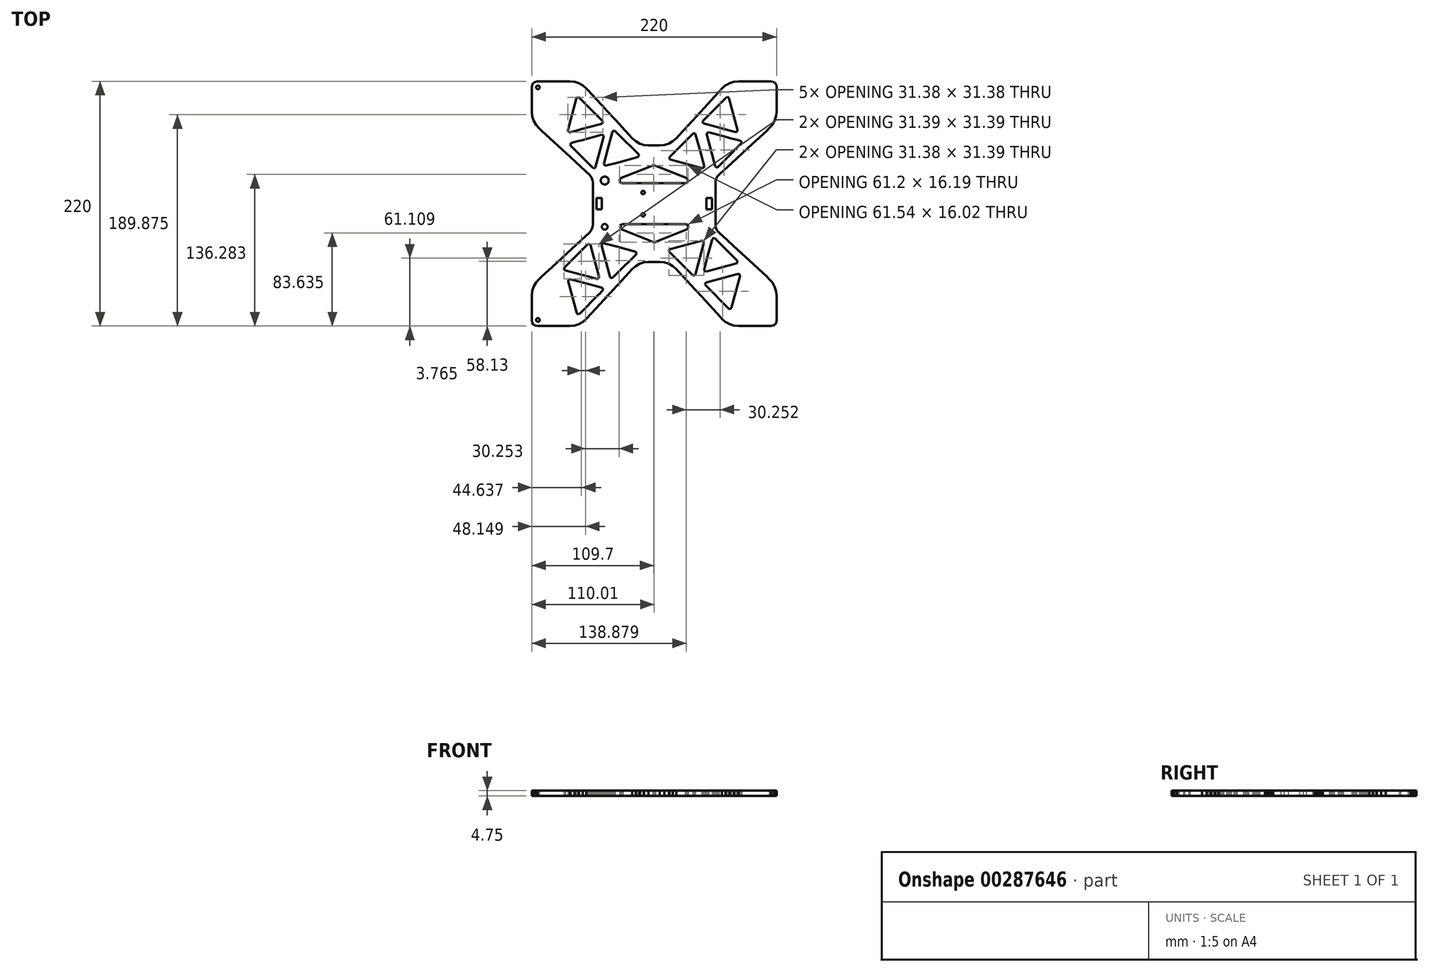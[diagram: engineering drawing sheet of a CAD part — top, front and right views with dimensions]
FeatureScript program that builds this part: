
annotation { "Feature Type Name" : "Feature", "Feature Type Description" : "" }
export const myFeature = defineFeature(function(context is Context, id is Id, definition is map)
    precondition{}
    {
        {
            var Q0;
            Q0=qCreatedBy(makeId("Top.planeOp"),FACE);
            var sketch = newSketch(context, id + "F0", { "sketchPlane" : qUnion([Q0])});
            skLineSegment(sketch, "E0", {"start": v(110, -105) * mm, "end": v(109.97, -105.11) * mm});
            skLineSegment(sketch, "E1", {"start": v(109.97, -105.11) * mm, "end": v(109.33, -107.5) * mm});
            skLineSegment(sketch, "E2", {"start": v(109.33, -107.5) * mm, "end": v(107.5, -109.33) * mm});
            skLineSegment(sketch, "E3", {"start": v(107.5, -109.33) * mm, "end": v(105.11, -109.97) * mm});
            skLineSegment(sketch, "E4", {"start": v(105.11, -109.97) * mm, "end": v(105, -110) * mm});
            skLineSegment(sketch, "E5", {"start": v(105, -110) * mm, "end": v(75.71, -110) * mm});
            skLineSegment(sketch, "E6", {"start": v(75.71, -110) * mm, "end": v(71.6, -109.58) * mm});
            skLineSegment(sketch, "E7", {"start": v(71.6, -109.58) * mm, "end": v(67.68, -108.32) * mm});
            skLineSegment(sketch, "E8", {"start": v(67.68, -108.32) * mm, "end": v(65.54, -107.1) * mm});
            skLineSegment(sketch, "E9", {"start": v(65.54, -107.1) * mm, "end": v(64.1, -106.29) * mm});
            skLineSegment(sketch, "E10", {"start": v(64.1, -106.29) * mm, "end": v(61, -103.56) * mm});
            skLineSegment(sketch, "E11", {"start": v(61, -103.56) * mm, "end": v(60.02, -102.49) * mm});
            skLineSegment(sketch, "E12", {"start": v(60.02, -102.49) * mm, "end": v(59.43, -101.85) * mm});
            skLineSegment(sketch, "E13", {"start": v(59.43, -101.85) * mm, "end": v(42.66, -83.66) * mm});
            skLineSegment(sketch, "E14", {"start": v(42.66, -83.66) * mm, "end": v(37.1, -77.62) * mm});
            skLineSegment(sketch, "E15", {"start": v(37.1, -77.62) * mm, "end": v(25.96, -65.54) * mm});
            skLineSegment(sketch, "E16", {"start": v(25.96, -65.54) * mm, "end": v(20.43, -59.54) * mm});
            skLineSegment(sketch, "E17", {"start": v(20.43, -59.54) * mm, "end": v(19.77, -58.82) * mm});
            skLineSegment(sketch, "E18", {"start": v(19.77, -58.82) * mm, "end": v(16.67, -56.1) * mm});
            skLineSegment(sketch, "E19", {"start": v(16.67, -56.1) * mm, "end": v(13.09, -54.06) * mm});
            skLineSegment(sketch, "E20", {"start": v(13.09, -54.06) * mm, "end": v(9.16, -52.8) * mm});
            skLineSegment(sketch, "E21", {"start": v(9.16, -52.8) * mm, "end": v(5.06, -52.37) * mm});
            skLineSegment(sketch, "E22", {"start": v(5.06, -52.37) * mm, "end": v(-5.06, -52.37) * mm});
            skLineSegment(sketch, "E23", {"start": v(-5.06, -52.37) * mm, "end": v(-9.16, -52.8) * mm});
            skLineSegment(sketch, "E24", {"start": v(-9.16, -52.8) * mm, "end": v(-13.1, -54.06) * mm});
            skLineSegment(sketch, "E25", {"start": v(-13.1, -54.06) * mm, "end": v(-16.67, -56.1) * mm});
            skLineSegment(sketch, "E26", {"start": v(-16.67, -56.1) * mm, "end": v(-19.77, -58.82) * mm});
            skLineSegment(sketch, "E27", {"start": v(-19.77, -58.82) * mm, "end": v(-25.96, -65.54) * mm});
            skLineSegment(sketch, "E28", {"start": v(-25.96, -65.54) * mm, "end": v(-32.77, -72.92) * mm});
            skLineSegment(sketch, "E29", {"start": v(-32.77, -72.92) * mm, "end": v(-37.77, -78.35) * mm});
            skLineSegment(sketch, "E30", {"start": v(-37.77, -78.35) * mm, "end": v(-38.62, -79.27) * mm});
            skLineSegment(sketch, "E31", {"start": v(-38.62, -79.27) * mm, "end": v(-39.42, -80.14) * mm});
            skLineSegment(sketch, "E32", {"start": v(-39.42, -80.14) * mm, "end": v(-41.06, -81.92) * mm});
            skLineSegment(sketch, "E33", {"start": v(-41.06, -81.92) * mm, "end": v(-56.16, -98.3) * mm});
            skLineSegment(sketch, "E34", {"start": v(-56.16, -98.3) * mm, "end": v(-61, -103.56) * mm});
            skLineSegment(sketch, "E35", {"start": v(-61, -103.56) * mm, "end": v(-64.1, -106.29) * mm});
            skLineSegment(sketch, "E36", {"start": v(-64.1, -106.29) * mm, "end": v(-65.54, -107.1) * mm});
            skLineSegment(sketch, "E37", {"start": v(-65.54, -107.1) * mm, "end": v(-67.68, -108.32) * mm});
            skLineSegment(sketch, "E38", {"start": v(-67.68, -108.32) * mm, "end": v(-71.6, -109.58) * mm});
            skLineSegment(sketch, "E39", {"start": v(-71.6, -109.58) * mm, "end": v(-75.71, -110) * mm});
            skLineSegment(sketch, "E40", {"start": v(-75.71, -110) * mm, "end": v(-105, -110) * mm});
            skLineSegment(sketch, "E41", {"start": v(-105, -110) * mm, "end": v(-106.91, -109.62) * mm});
            skLineSegment(sketch, "E42", {"start": v(-106.91, -109.62) * mm, "end": v(-108.53, -108.54) * mm});
            skLineSegment(sketch, "E43", {"start": v(-108.53, -108.54) * mm, "end": v(-109.62, -106.92) * mm});
            skLineSegment(sketch, "E44", {"start": v(-109.62, -106.92) * mm, "end": v(-110, -105) * mm});
            skLineSegment(sketch, "E45", {"start": v(-110, -105) * mm, "end": v(-110, -82.51) * mm});
            skLineSegment(sketch, "E46", {"start": v(-110, -82.51) * mm, "end": v(-109.58, -78.41) * mm});
            skLineSegment(sketch, "E47", {"start": v(-109.58, -78.41) * mm, "end": v(-108.32, -74.48) * mm});
            skLineSegment(sketch, "E48", {"start": v(-108.32, -74.48) * mm, "end": v(-106.28, -70.9) * mm});
            skLineSegment(sketch, "E49", {"start": v(-106.28, -70.9) * mm, "end": v(-103.55, -67.8) * mm});
            skLineSegment(sketch, "E50", {"start": v(-103.55, -67.8) * mm, "end": v(-101.1, -65.54) * mm});
            skLineSegment(sketch, "E51", {"start": v(-101.1, -65.54) * mm, "end": v(-91.63, -56.8) * mm});
            skLineSegment(sketch, "E52", {"start": v(-91.63, -56.8) * mm, "end": v(-65.54, -32.76) * mm});
            skLineSegment(sketch, "E53", {"start": v(-65.54, -32.76) * mm, "end": v(-58.22, -26.01) * mm});
            skLineSegment(sketch, "E54", {"start": v(-58.22, -26.01) * mm, "end": v(-56.86, -24.47) * mm});
            skLineSegment(sketch, "E55", {"start": v(-56.86, -24.47) * mm, "end": v(-55.84, -22.68) * mm});
            skLineSegment(sketch, "E56", {"start": v(-55.84, -22.68) * mm, "end": v(-55.21, -20.71) * mm});
            skLineSegment(sketch, "E57", {"start": v(-55.21, -20.71) * mm, "end": v(-55, -18.66) * mm});
            skLineSegment(sketch, "E58", {"start": v(-55, -18.66) * mm, "end": v(-55, 18.67) * mm});
            skLineSegment(sketch, "E59", {"start": v(-55, 18.67) * mm, "end": v(-55.21, 20.72) * mm});
            skLineSegment(sketch, "E60", {"start": v(-55.21, 20.72) * mm, "end": v(-55.84, 22.68) * mm});
            skLineSegment(sketch, "E61", {"start": v(-55.84, 22.68) * mm, "end": v(-56.86, 24.47) * mm});
            skLineSegment(sketch, "E62", {"start": v(-56.86, 24.47) * mm, "end": v(-58.22, 26.02) * mm});
            skLineSegment(sketch, "E63", {"start": v(-58.22, 26.02) * mm, "end": v(-65.54, 32.76) * mm});
            skLineSegment(sketch, "E64", {"start": v(-65.54, 32.76) * mm, "end": v(-66.26, 33.43) * mm});
            skLineSegment(sketch, "E65", {"start": v(-66.26, 33.43) * mm, "end": v(-75.44, 41.9) * mm});
            skLineSegment(sketch, "E66", {"start": v(-75.44, 41.9) * mm, "end": v(-101.1, 65.54) * mm});
            skLineSegment(sketch, "E67", {"start": v(-101.1, 65.54) * mm, "end": v(-103.55, 67.8) * mm});
            skLineSegment(sketch, "E68", {"start": v(-103.55, 67.8) * mm, "end": v(-106.28, 70.9) * mm});
            skLineSegment(sketch, "E69", {"start": v(-106.28, 70.9) * mm, "end": v(-108.32, 74.48) * mm});
            skLineSegment(sketch, "E70", {"start": v(-108.32, 74.48) * mm, "end": v(-109.58, 78.41) * mm});
            skLineSegment(sketch, "E71", {"start": v(-109.58, 78.41) * mm, "end": v(-110, 82.51) * mm});
            skLineSegment(sketch, "E72", {"start": v(-110, 82.51) * mm, "end": v(-110, 105) * mm});
            skLineSegment(sketch, "E73", {"start": v(-110, 105) * mm, "end": v(-109.97, 105.12) * mm});
            skLineSegment(sketch, "E74", {"start": v(-109.97, 105.12) * mm, "end": v(-109.33, 107.5) * mm});
            skLineSegment(sketch, "E75", {"start": v(-109.33, 107.5) * mm, "end": v(-108.87, 107.96) * mm});
            skLineSegment(sketch, "E76", {"start": v(-108.87, 107.96) * mm, "end": v(-107.5, 109.33) * mm});
            skLineSegment(sketch, "E77", {"start": v(-107.5, 109.33) * mm, "end": v(-105.11, 109.97) * mm});
            skLineSegment(sketch, "E78", {"start": v(-105.11, 109.97) * mm, "end": v(-105, 110) * mm});
            skLineSegment(sketch, "E79", {"start": v(-105, 110) * mm, "end": v(-75.71, 110) * mm});
            skLineSegment(sketch, "E80", {"start": v(-75.71, 110) * mm, "end": v(-71.6, 109.58) * mm});
            skLineSegment(sketch, "E81", {"start": v(-71.6, 109.58) * mm, "end": v(-67.68, 108.32) * mm});
            skLineSegment(sketch, "E82", {"start": v(-67.68, 108.32) * mm, "end": v(-65.54, 107.1) * mm});
            skLineSegment(sketch, "E83", {"start": v(-65.54, 107.1) * mm, "end": v(-64.1, 106.29) * mm});
            skLineSegment(sketch, "E84", {"start": v(-64.1, 106.29) * mm, "end": v(-61, 103.56) * mm});
            skLineSegment(sketch, "E85", {"start": v(-61, 103.56) * mm, "end": v(-59.4, 101.81) * mm});
            skLineSegment(sketch, "E86", {"start": v(-59.4, 101.81) * mm, "end": v(-43.95, 85.06) * mm});
            skLineSegment(sketch, "E87", {"start": v(-43.95, 85.06) * mm, "end": v(-42.3, 83.27) * mm});
            skLineSegment(sketch, "E88", {"start": v(-42.3, 83.27) * mm, "end": v(-34.8, 75.14) * mm});
            skLineSegment(sketch, "E89", {"start": v(-34.8, 75.14) * mm, "end": v(-25.96, 65.54) * mm});
            skLineSegment(sketch, "E90", {"start": v(-25.96, 65.54) * mm, "end": v(-19.77, 58.82) * mm});
            skLineSegment(sketch, "E91", {"start": v(-19.77, 58.82) * mm, "end": v(-16.67, 56.1) * mm});
            skLineSegment(sketch, "E92", {"start": v(-16.67, 56.1) * mm, "end": v(-13.1, 54.06) * mm});
            skLineSegment(sketch, "E93", {"start": v(-13.1, 54.06) * mm, "end": v(-9.16, 52.8) * mm});
            skLineSegment(sketch, "E94", {"start": v(-9.16, 52.8) * mm, "end": v(-5.06, 52.38) * mm});
            skLineSegment(sketch, "E95", {"start": v(-5.06, 52.38) * mm, "end": v(5.06, 52.38) * mm});
            skLineSegment(sketch, "E96", {"start": v(5.06, 52.38) * mm, "end": v(9.16, 52.8) * mm});
            skLineSegment(sketch, "E97", {"start": v(9.16, 52.8) * mm, "end": v(13.09, 54.06) * mm});
            skLineSegment(sketch, "E98", {"start": v(13.09, 54.06) * mm, "end": v(16.67, 56.1) * mm});
            skLineSegment(sketch, "E99", {"start": v(16.67, 56.1) * mm, "end": v(19.77, 58.82) * mm});
            skLineSegment(sketch, "E100", {"start": v(19.77, 58.82) * mm, "end": v(25.96, 65.54) * mm});
            skLineSegment(sketch, "E101", {"start": v(25.96, 65.54) * mm, "end": v(34.46, 74.76) * mm});
            skLineSegment(sketch, "E102", {"start": v(34.46, 74.76) * mm, "end": v(45, 86.2) * mm});
            skLineSegment(sketch, "E103", {"start": v(45, 86.2) * mm, "end": v(61, 103.56) * mm});
            skLineSegment(sketch, "E104", {"start": v(61, 103.56) * mm, "end": v(64.1, 106.29) * mm});
            skLineSegment(sketch, "E105", {"start": v(64.1, 106.29) * mm, "end": v(65.54, 107.1) * mm});
            skLineSegment(sketch, "E106", {"start": v(65.54, 107.1) * mm, "end": v(67.68, 108.32) * mm});
            skLineSegment(sketch, "E107", {"start": v(67.68, 108.32) * mm, "end": v(71.6, 109.58) * mm});
            skLineSegment(sketch, "E108", {"start": v(71.6, 109.58) * mm, "end": v(75.71, 110) * mm});
            skLineSegment(sketch, "E109", {"start": v(75.71, 110) * mm, "end": v(105, 110) * mm});
            skLineSegment(sketch, "E110", {"start": v(105, 110) * mm, "end": v(106.91, 109.62) * mm});
            skLineSegment(sketch, "E111", {"start": v(106.91, 109.62) * mm, "end": v(107.98, 108.9) * mm});
            skLineSegment(sketch, "E112", {"start": v(107.98, 108.9) * mm, "end": v(108.53, 108.54) * mm});
            skLineSegment(sketch, "E113", {"start": v(108.53, 108.54) * mm, "end": v(109.62, 106.92) * mm});
            skLineSegment(sketch, "E114", {"start": v(109.62, 106.92) * mm, "end": v(109.98, 105.13) * mm});
            skLineSegment(sketch, "E115", {"start": v(109.98, 105.13) * mm, "end": v(110, 105) * mm});
            skLineSegment(sketch, "E116", {"start": v(110, 105) * mm, "end": v(110, 82.51) * mm});
            skLineSegment(sketch, "E117", {"start": v(110, 82.51) * mm, "end": v(109.58, 78.41) * mm});
            skLineSegment(sketch, "E118", {"start": v(109.58, 78.41) * mm, "end": v(108.32, 74.48) * mm});
            skLineSegment(sketch, "E119", {"start": v(108.32, 74.48) * mm, "end": v(106.28, 70.9) * mm});
            skLineSegment(sketch, "E120", {"start": v(106.28, 70.9) * mm, "end": v(103.56, 67.8) * mm});
            skLineSegment(sketch, "E121", {"start": v(103.56, 67.8) * mm, "end": v(101.1, 65.54) * mm});
            skLineSegment(sketch, "E122", {"start": v(101.1, 65.54) * mm, "end": v(88.12, 53.58) * mm});
            skLineSegment(sketch, "E123", {"start": v(88.12, 53.58) * mm, "end": v(65.54, 32.76) * mm});
            skLineSegment(sketch, "E124", {"start": v(65.54, 32.76) * mm, "end": v(63.4, 30.8) * mm});
            skLineSegment(sketch, "E125", {"start": v(63.4, 30.8) * mm, "end": v(58.22, 26.02) * mm});
            skLineSegment(sketch, "E126", {"start": v(58.22, 26.02) * mm, "end": v(56.86, 24.47) * mm});
            skLineSegment(sketch, "E127", {"start": v(56.86, 24.47) * mm, "end": v(55.84, 22.68) * mm});
            skLineSegment(sketch, "E128", {"start": v(55.84, 22.68) * mm, "end": v(55.21, 20.72) * mm});
            skLineSegment(sketch, "E129", {"start": v(55.21, 20.72) * mm, "end": v(55, 18.67) * mm});
            skLineSegment(sketch, "E130", {"start": v(55, 18.67) * mm, "end": v(55, -18.66) * mm});
            skLineSegment(sketch, "E131", {"start": v(55, -18.66) * mm, "end": v(55.21, -20.71) * mm});
            skLineSegment(sketch, "E132", {"start": v(55.21, -20.71) * mm, "end": v(55.84, -22.68) * mm});
            skLineSegment(sketch, "E133", {"start": v(55.84, -22.68) * mm, "end": v(56.86, -24.47) * mm});
            skLineSegment(sketch, "E134", {"start": v(56.86, -24.47) * mm, "end": v(58.22, -26.01) * mm});
            skLineSegment(sketch, "E135", {"start": v(58.22, -26.01) * mm, "end": v(65.54, -32.76) * mm});
            skLineSegment(sketch, "E136", {"start": v(65.54, -32.76) * mm, "end": v(66.29, -33.45) * mm});
            skLineSegment(sketch, "E137", {"start": v(66.29, -33.45) * mm, "end": v(75, -41.48) * mm});
            skLineSegment(sketch, "E138", {"start": v(75, -41.48) * mm, "end": v(81.72, -47.68) * mm});
            skLineSegment(sketch, "E139", {"start": v(81.72, -47.68) * mm, "end": v(101.1, -65.54) * mm});
            skLineSegment(sketch, "E140", {"start": v(101.1, -65.54) * mm, "end": v(103.56, -67.8) * mm});
            skLineSegment(sketch, "E141", {"start": v(103.56, -67.8) * mm, "end": v(106.28, -70.9) * mm});
            skLineSegment(sketch, "E142", {"start": v(106.28, -70.9) * mm, "end": v(108.32, -74.48) * mm});
            skLineSegment(sketch, "E143", {"start": v(108.32, -74.48) * mm, "end": v(109.58, -78.41) * mm});
            skLineSegment(sketch, "E144", {"start": v(109.58, -78.41) * mm, "end": v(110, -82.51) * mm});
            skLineSegment(sketch, "E145", {"start": v(110, -82.51) * mm, "end": v(110, -105) * mm});
            skLineSegment(sketch, "E146", {"start": v(-43.2, 34.18) * mm, "end": v(-32.77, 36.98) * mm});
            skLineSegment(sketch, "E147", {"start": v(-32.77, 36.98) * mm, "end": v(-14.76, 41.8) * mm});
            skLineSegment(sketch, "E148", {"start": v(-14.76, 41.8) * mm, "end": v(-13.92, 42.4) * mm});
            skLineSegment(sketch, "E149", {"start": v(-13.92, 42.4) * mm, "end": v(-13.66, 43.38) * mm});
            skLineSegment(sketch, "E150", {"start": v(-13.66, 43.38) * mm, "end": v(-14.1, 44.31) * mm});
            skLineSegment(sketch, "E151", {"start": v(-14.1, 44.31) * mm, "end": v(-32.77, 62.99) * mm});
            skLineSegment(sketch, "E152", {"start": v(-32.77, 62.99) * mm, "end": v(-34.9, 65.12) * mm});
            skLineSegment(sketch, "E153", {"start": v(-34.9, 65.12) * mm, "end": v(-34.91, 65.13) * mm});
            skLineSegment(sketch, "E154", {"start": v(-34.91, 65.13) * mm, "end": v(-35.78, 65.54) * mm});
            skLineSegment(sketch, "E155", {"start": v(-35.78, 65.54) * mm, "end": v(-35.84, 65.57) * mm});
            skLineSegment(sketch, "E156", {"start": v(-35.84, 65.57) * mm, "end": v(-35.95, 65.54) * mm});
            skLineSegment(sketch, "E157", {"start": v(-35.95, 65.54) * mm, "end": v(-36.83, 65.3) * mm});
            skLineSegment(sketch, "E158", {"start": v(-36.83, 65.3) * mm, "end": v(-37.42, 64.46) * mm});
            skLineSegment(sketch, "E159", {"start": v(-37.42, 64.46) * mm, "end": v(-37.43, 64.44) * mm});
            skLineSegment(sketch, "E160", {"start": v(-37.43, 64.44) * mm, "end": v(-41.52, 49.15) * mm});
            skLineSegment(sketch, "E161", {"start": v(-41.52, 49.15) * mm, "end": v(-45.04, 36.02) * mm});
            skLineSegment(sketch, "E162", {"start": v(-45.04, 36.02) * mm, "end": v(-44.95, 35) * mm});
            skLineSegment(sketch, "E163", {"start": v(-44.95, 35) * mm, "end": v(-44.23, 34.27) * mm});
            skLineSegment(sketch, "E164", {"start": v(-44.23, 34.27) * mm, "end": v(-43.2, 34.18) * mm});
            skLineSegment(sketch, "E165", {"start": v(-58.87, -36.18) * mm, "end": v(-59.8, -36.61) * mm});
            skLineSegment(sketch, "E166", {"start": v(-59.8, -36.61) * mm, "end": v(-65.54, -42.35) * mm});
            skLineSegment(sketch, "E167", {"start": v(-65.54, -42.35) * mm, "end": v(-80.62, -57.43) * mm});
            skLineSegment(sketch, "E168", {"start": v(-80.62, -57.43) * mm, "end": v(-81.06, -58.36) * mm});
            skLineSegment(sketch, "E169", {"start": v(-81.06, -58.36) * mm, "end": v(-80.79, -59.35) * mm});
            skLineSegment(sketch, "E170", {"start": v(-80.79, -59.35) * mm, "end": v(-79.95, -59.94) * mm});
            skLineSegment(sketch, "E171", {"start": v(-79.95, -59.94) * mm, "end": v(-65.54, -63.8) * mm});
            skLineSegment(sketch, "E172", {"start": v(-65.54, -63.8) * mm, "end": v(-59.07, -65.54) * mm});
            skLineSegment(sketch, "E173", {"start": v(-59.07, -65.54) * mm, "end": v(-51.5, -67.56) * mm});
            skLineSegment(sketch, "E174", {"start": v(-51.5, -67.56) * mm, "end": v(-50.49, -67.47) * mm});
            skLineSegment(sketch, "E175", {"start": v(-50.49, -67.47) * mm, "end": v(-49.76, -66.75) * mm});
            skLineSegment(sketch, "E176", {"start": v(-49.76, -66.75) * mm, "end": v(-49.67, -65.73) * mm});
            skLineSegment(sketch, "E177", {"start": v(-49.67, -65.73) * mm, "end": v(-49.72, -65.54) * mm});
            skLineSegment(sketch, "E178", {"start": v(-49.72, -65.54) * mm, "end": v(-49.74, -65.46) * mm});
            skLineSegment(sketch, "E179", {"start": v(-49.74, -65.46) * mm, "end": v(-55.38, -44.43) * mm});
            skLineSegment(sketch, "E180", {"start": v(-55.38, -44.43) * mm, "end": v(-57.3, -37.28) * mm});
            skLineSegment(sketch, "E181", {"start": v(-57.3, -37.28) * mm, "end": v(-57.81, -36.53) * mm});
            skLineSegment(sketch, "E182", {"start": v(-57.81, -36.53) * mm, "end": v(-57.88, -36.44) * mm});
            skLineSegment(sketch, "E183", {"start": v(-57.88, -36.44) * mm, "end": v(-58.87, -36.18) * mm});
            skLineSegment(sketch, "E184", {"start": v(65.54, 66.43) * mm, "end": v(68.87, 65.54) * mm});
            skLineSegment(sketch, "E185", {"start": v(68.87, 65.54) * mm, "end": v(72.99, 64.43) * mm});
            skLineSegment(sketch, "E186", {"start": v(72.99, 64.43) * mm, "end": v(74, 64.52) * mm});
            skLineSegment(sketch, "E187", {"start": v(74, 64.52) * mm, "end": v(74.73, 65.25) * mm});
            skLineSegment(sketch, "E188", {"start": v(74.73, 65.25) * mm, "end": v(74.76, 65.54) * mm});
            skLineSegment(sketch, "E189", {"start": v(74.76, 65.54) * mm, "end": v(74.82, 66.27) * mm});
            skLineSegment(sketch, "E190", {"start": v(74.82, 66.27) * mm, "end": v(67.2, 94.71) * mm});
            skLineSegment(sketch, "E191", {"start": v(67.2, 94.71) * mm, "end": v(66.62, 95.55) * mm});
            skLineSegment(sketch, "E192", {"start": v(66.62, 95.55) * mm, "end": v(65.62, 95.82) * mm});
            skLineSegment(sketch, "E193", {"start": v(65.62, 95.82) * mm, "end": v(65.54, 95.78) * mm});
            skLineSegment(sketch, "E194", {"start": v(65.54, 95.78) * mm, "end": v(64.7, 95.39) * mm});
            skLineSegment(sketch, "E195", {"start": v(64.7, 95.39) * mm, "end": v(43.87, 74.57) * mm});
            skLineSegment(sketch, "E196", {"start": v(43.87, 74.57) * mm, "end": v(43.44, 73.64) * mm});
            skLineSegment(sketch, "E197", {"start": v(43.44, 73.64) * mm, "end": v(43.7, 72.65) * mm});
            skLineSegment(sketch, "E198", {"start": v(43.7, 72.65) * mm, "end": v(44.55, 72.06) * mm});
            skLineSegment(sketch, "E199", {"start": v(44.55, 72.06) * mm, "end": v(65.54, 66.43) * mm});
            skLineSegment(sketch, "E200", {"start": v(-17.01, -43.07) * mm, "end": v(-32.77, -38.85) * mm});
            skLineSegment(sketch, "E201", {"start": v(-32.77, -38.85) * mm, "end": v(-45.45, -35.45) * mm});
            skLineSegment(sketch, "E202", {"start": v(-45.45, -35.45) * mm, "end": v(-46.48, -35.54) * mm});
            skLineSegment(sketch, "E203", {"start": v(-46.48, -35.54) * mm, "end": v(-47.2, -36.26) * mm});
            skLineSegment(sketch, "E204", {"start": v(-47.2, -36.26) * mm, "end": v(-47.3, -37.28) * mm});
            skLineSegment(sketch, "E205", {"start": v(-47.3, -37.28) * mm, "end": v(-39.72, -65.54) * mm});
            skLineSegment(sketch, "E206", {"start": v(-39.72, -65.54) * mm, "end": v(-39.67, -65.73) * mm});
            skLineSegment(sketch, "E207", {"start": v(-39.67, -65.73) * mm, "end": v(-39.08, -66.57) * mm});
            skLineSegment(sketch, "E208", {"start": v(-39.08, -66.57) * mm, "end": v(-38.1, -66.83) * mm});
            skLineSegment(sketch, "E209", {"start": v(-38.1, -66.83) * mm, "end": v(-37.16, -66.4) * mm});
            skLineSegment(sketch, "E210", {"start": v(-37.16, -66.4) * mm, "end": v(-36.3, -65.54) * mm});
            skLineSegment(sketch, "E211", {"start": v(-36.3, -65.54) * mm, "end": v(-32.77, -62) * mm});
            skLineSegment(sketch, "E212", {"start": v(-32.77, -62) * mm, "end": v(-16.34, -45.58) * mm});
            skLineSegment(sketch, "E213", {"start": v(-16.34, -45.58) * mm, "end": v(-15.9, -44.65) * mm});
            skLineSegment(sketch, "E214", {"start": v(-15.9, -44.65) * mm, "end": v(-16.17, -43.65) * mm});
            skLineSegment(sketch, "E215", {"start": v(-16.17, -43.65) * mm, "end": v(-17.01, -43.07) * mm});
            skLineSegment(sketch, "E216", {"start": v(78.32, 55.84) * mm, "end": v(77.48, 56.43) * mm});
            skLineSegment(sketch, "E217", {"start": v(77.48, 56.43) * mm, "end": v(74.05, 57.35) * mm});
            skLineSegment(sketch, "E218", {"start": v(74.05, 57.35) * mm, "end": v(68.35, 58.88) * mm});
            skLineSegment(sketch, "E219", {"start": v(68.35, 58.88) * mm, "end": v(65.54, 59.63) * mm});
            skLineSegment(sketch, "E220", {"start": v(65.54, 59.63) * mm, "end": v(49.04, 64.05) * mm});
            skLineSegment(sketch, "E221", {"start": v(49.04, 64.05) * mm, "end": v(48.02, 63.96) * mm});
            skLineSegment(sketch, "E222", {"start": v(48.02, 63.96) * mm, "end": v(47.3, 63.24) * mm});
            skLineSegment(sketch, "E223", {"start": v(47.3, 63.24) * mm, "end": v(47.2, 62.21) * mm});
            skLineSegment(sketch, "E224", {"start": v(47.2, 62.21) * mm, "end": v(50.7, 49.15) * mm});
            skLineSegment(sketch, "E225", {"start": v(50.7, 49.15) * mm, "end": v(54.82, 33.77) * mm});
            skLineSegment(sketch, "E226", {"start": v(54.82, 33.77) * mm, "end": v(55.41, 32.93) * mm});
            skLineSegment(sketch, "E227", {"start": v(55.41, 32.93) * mm, "end": v(56.02, 32.77) * mm});
            skLineSegment(sketch, "E228", {"start": v(56.02, 32.77) * mm, "end": v(56.4, 32.66) * mm});
            skLineSegment(sketch, "E229", {"start": v(56.4, 32.66) * mm, "end": v(56.62, 32.77) * mm});
            skLineSegment(sketch, "E230", {"start": v(56.62, 32.77) * mm, "end": v(57.33, 33.1) * mm});
            skLineSegment(sketch, "E231", {"start": v(57.33, 33.1) * mm, "end": v(65.54, 41.3) * mm});
            skLineSegment(sketch, "E232", {"start": v(65.54, 41.3) * mm, "end": v(78.16, 53.92) * mm});
            skLineSegment(sketch, "E233", {"start": v(78.16, 53.92) * mm, "end": v(78.59, 54.85) * mm});
            skLineSegment(sketch, "E234", {"start": v(78.59, 54.85) * mm, "end": v(78.32, 55.84) * mm});
            skLineSegment(sketch, "E235", {"start": v(-53.26, 32.1) * mm, "end": v(-52.79, 32.77) * mm});
            skLineSegment(sketch, "E236", {"start": v(-52.79, 32.77) * mm, "end": v(-52.67, 32.94) * mm});
            skLineSegment(sketch, "E237", {"start": v(-52.67, 32.94) * mm, "end": v(-48.33, 49.15) * mm});
            skLineSegment(sketch, "E238", {"start": v(-48.33, 49.15) * mm, "end": v(-45.43, 59.97) * mm});
            skLineSegment(sketch, "E239", {"start": v(-45.43, 59.97) * mm, "end": v(-45.52, 60.99) * mm});
            skLineSegment(sketch, "E240", {"start": v(-45.52, 60.99) * mm, "end": v(-46.24, 61.71) * mm});
            skLineSegment(sketch, "E241", {"start": v(-46.24, 61.71) * mm, "end": v(-47.26, 61.8) * mm});
            skLineSegment(sketch, "E242", {"start": v(-47.26, 61.8) * mm, "end": v(-65.54, 56.9) * mm});
            skLineSegment(sketch, "E243", {"start": v(-65.54, 56.9) * mm, "end": v(-68.56, 56.1) * mm});
            skLineSegment(sketch, "E244", {"start": v(-68.56, 56.1) * mm, "end": v(-74.3, 54.56) * mm});
            skLineSegment(sketch, "E245", {"start": v(-74.3, 54.56) * mm, "end": v(-75.13, 53.97) * mm});
            skLineSegment(sketch, "E246", {"start": v(-75.13, 53.97) * mm, "end": v(-75.4, 52.98) * mm});
            skLineSegment(sketch, "E247", {"start": v(-75.4, 52.98) * mm, "end": v(-74.96, 52.05) * mm});
            skLineSegment(sketch, "E248", {"start": v(-74.96, 52.05) * mm, "end": v(-65.54, 42.63) * mm});
            skLineSegment(sketch, "E249", {"start": v(-65.54, 42.63) * mm, "end": v(-55.68, 32.77) * mm});
            skLineSegment(sketch, "E250", {"start": v(-55.68, 32.77) * mm, "end": v(-55.18, 32.27) * mm});
            skLineSegment(sketch, "E251", {"start": v(-55.18, 32.27) * mm, "end": v(-54.25, 31.83) * mm});
            skLineSegment(sketch, "E252", {"start": v(-54.25, 31.83) * mm, "end": v(-53.26, 32.1) * mm});
            skLineSegment(sketch, "E253", {"start": v(-75.7, 64.18) * mm, "end": v(-70.65, 65.54) * mm});
            skLineSegment(sketch, "E254", {"start": v(-70.65, 65.54) * mm, "end": v(-65.54, 66.9) * mm});
            skLineSegment(sketch, "E255", {"start": v(-65.54, 66.9) * mm, "end": v(-48.52, 71.47) * mm});
            skLineSegment(sketch, "E256", {"start": v(-48.52, 71.47) * mm, "end": v(-47.26, 71.8) * mm});
            skLineSegment(sketch, "E257", {"start": v(-47.26, 71.8) * mm, "end": v(-46.42, 72.4) * mm});
            skLineSegment(sketch, "E258", {"start": v(-46.42, 72.4) * mm, "end": v(-46.16, 73.38) * mm});
            skLineSegment(sketch, "E259", {"start": v(-46.16, 73.38) * mm, "end": v(-46.6, 74.31) * mm});
            skLineSegment(sketch, "E260", {"start": v(-46.6, 74.31) * mm, "end": v(-67.41, 95.13) * mm});
            skLineSegment(sketch, "E261", {"start": v(-67.41, 95.13) * mm, "end": v(-68.34, 95.57) * mm});
            skLineSegment(sketch, "E262", {"start": v(-68.34, 95.57) * mm, "end": v(-69.33, 95.3) * mm});
            skLineSegment(sketch, "E263", {"start": v(-69.33, 95.3) * mm, "end": v(-69.92, 94.46) * mm});
            skLineSegment(sketch, "E264", {"start": v(-69.92, 94.46) * mm, "end": v(-77.54, 66.02) * mm});
            skLineSegment(sketch, "E265", {"start": v(-77.54, 66.02) * mm, "end": v(-77.5, 65.54) * mm});
            skLineSegment(sketch, "E266", {"start": v(-77.5, 65.54) * mm, "end": v(-77.45, 65) * mm});
            skLineSegment(sketch, "E267", {"start": v(-77.45, 65) * mm, "end": v(-76.73, 64.27) * mm});
            skLineSegment(sketch, "E268", {"start": v(-76.73, 64.27) * mm, "end": v(-75.7, 64.18) * mm});
            skLineSegment(sketch, "E269", {"start": v(30.35, -22.02) * mm, "end": v(30.61, -20.32) * mm});
            skLineSegment(sketch, "E270", {"start": v(30.61, -20.32) * mm, "end": v(29.73, -18.85) * mm});
            skLineSegment(sketch, "E271", {"start": v(29.73, -18.85) * mm, "end": v(28.12, -18.27) * mm});
            skLineSegment(sketch, "E272", {"start": v(28.12, -18.27) * mm, "end": v(-28.1, -18.27) * mm});
            skLineSegment(sketch, "E273", {"start": v(-28.1, -18.27) * mm, "end": v(-29.72, -18.85) * mm});
            skLineSegment(sketch, "E274", {"start": v(-29.72, -18.85) * mm, "end": v(-30.6, -20.33) * mm});
            skLineSegment(sketch, "E275", {"start": v(-30.6, -20.33) * mm, "end": v(-30.33, -22.02) * mm});
            skLineSegment(sketch, "E276", {"start": v(-30.33, -22.02) * mm, "end": v(-29.04, -23.16) * mm});
            skLineSegment(sketch, "E277", {"start": v(-29.04, -23.16) * mm, "end": v(-5.1, -32.77) * mm});
            skLineSegment(sketch, "E278", {"start": v(-5.1, -32.77) * mm, "end": v(-3.98, -33.22) * mm});
            skLineSegment(sketch, "E279", {"start": v(-3.98, -33.22) * mm, "end": v(-0.88, -34.46) * mm});
            skLineSegment(sketch, "E280", {"start": v(-0.88, -34.46) * mm, "end": v(0, -34.46) * mm});
            skLineSegment(sketch, "E281", {"start": v(0, -34.46) * mm, "end": v(1.01, -34.46) * mm});
            skLineSegment(sketch, "E282", {"start": v(1.01, -34.46) * mm, "end": v(3.68, -33.39) * mm});
            skLineSegment(sketch, "E283", {"start": v(3.68, -33.39) * mm, "end": v(5.22, -32.77) * mm});
            skLineSegment(sketch, "E284", {"start": v(5.22, -32.77) * mm, "end": v(29.07, -23.16) * mm});
            skLineSegment(sketch, "E285", {"start": v(29.07, -23.16) * mm, "end": v(30.35, -22.02) * mm});
            skLineSegment(sketch, "E286", {"start": v(-52, 5) * mm, "end": v(-52, -5) * mm});
            skLineSegment(sketch, "E287", {"start": v(-52, -5) * mm, "end": v(-47, -5) * mm});
            skLineSegment(sketch, "E288", {"start": v(-47, -5) * mm, "end": v(-47, 5) * mm});
            skLineSegment(sketch, "E289", {"start": v(-47, 5) * mm, "end": v(-52, 5) * mm});
            skLineSegment(sketch, "E290", {"start": v(75.23, -63.2) * mm, "end": v(66.52, -65.54) * mm});
            skLineSegment(sketch, "E291", {"start": v(66.52, -65.54) * mm, "end": v(65.54, -65.8) * mm});
            skLineSegment(sketch, "E292", {"start": v(65.54, -65.8) * mm, "end": v(46.8, -70.82) * mm});
            skLineSegment(sketch, "E293", {"start": v(46.8, -70.82) * mm, "end": v(45.95, -71.4) * mm});
            skLineSegment(sketch, "E294", {"start": v(45.95, -71.4) * mm, "end": v(45.69, -72.4) * mm});
            skLineSegment(sketch, "E295", {"start": v(45.69, -72.4) * mm, "end": v(46.12, -73.33) * mm});
            skLineSegment(sketch, "E296", {"start": v(46.12, -73.33) * mm, "end": v(66.94, -94.15) * mm});
            skLineSegment(sketch, "E297", {"start": v(66.94, -94.15) * mm, "end": v(67.87, -94.58) * mm});
            skLineSegment(sketch, "E298", {"start": v(67.87, -94.58) * mm, "end": v(68.86, -94.32) * mm});
            skLineSegment(sketch, "E299", {"start": v(68.86, -94.32) * mm, "end": v(69.45, -93.48) * mm});
            skLineSegment(sketch, "E300", {"start": v(69.45, -93.48) * mm, "end": v(76.94, -65.54) * mm});
            skLineSegment(sketch, "E301", {"start": v(76.94, -65.54) * mm, "end": v(77.07, -65.04) * mm});
            skLineSegment(sketch, "E302", {"start": v(77.07, -65.04) * mm, "end": v(76.98, -64.01) * mm});
            skLineSegment(sketch, "E303", {"start": v(76.98, -64.01) * mm, "end": v(76.26, -63.29) * mm});
            skLineSegment(sketch, "E304", {"start": v(76.26, -63.29) * mm, "end": v(75.23, -63.2) * mm});
            skLineSegment(sketch, "E305", {"start": v(-46.17, -76.16) * mm, "end": v(-46.61, -75.85) * mm});
            skLineSegment(sketch, "E306", {"start": v(-46.61, -75.85) * mm, "end": v(-47.01, -75.57) * mm});
            skLineSegment(sketch, "E307", {"start": v(-47.01, -75.57) * mm, "end": v(-49.15, -75) * mm});
            skLineSegment(sketch, "E308", {"start": v(-49.15, -75) * mm, "end": v(-65.54, -70.6) * mm});
            skLineSegment(sketch, "E309", {"start": v(-65.54, -70.6) * mm, "end": v(-75.45, -67.95) * mm});
            skLineSegment(sketch, "E310", {"start": v(-75.45, -67.95) * mm, "end": v(-76.48, -68.04) * mm});
            skLineSegment(sketch, "E311", {"start": v(-76.48, -68.04) * mm, "end": v(-77.2, -68.76) * mm});
            skLineSegment(sketch, "E312", {"start": v(-77.2, -68.76) * mm, "end": v(-77.3, -69.79) * mm});
            skLineSegment(sketch, "E313", {"start": v(-77.3, -69.79) * mm, "end": v(-69.67, -98.23) * mm});
            skLineSegment(sketch, "E314", {"start": v(-69.67, -98.23) * mm, "end": v(-69.61, -98.3) * mm});
            skLineSegment(sketch, "E315", {"start": v(-69.61, -98.3) * mm, "end": v(-69.08, -99.07) * mm});
            skLineSegment(sketch, "E316", {"start": v(-69.08, -99.07) * mm, "end": v(-68.1, -99.33) * mm});
            skLineSegment(sketch, "E317", {"start": v(-68.1, -99.33) * mm, "end": v(-67.16, -98.9) * mm});
            skLineSegment(sketch, "E318", {"start": v(-67.16, -98.9) * mm, "end": v(-66.56, -98.3) * mm});
            skLineSegment(sketch, "E319", {"start": v(-66.56, -98.3) * mm, "end": v(-50.18, -81.92) * mm});
            skLineSegment(sketch, "E320", {"start": v(-50.18, -81.92) * mm, "end": v(-49.15, -80.89) * mm});
            skLineSegment(sketch, "E321", {"start": v(-49.15, -80.89) * mm, "end": v(-46.34, -78.08) * mm});
            skLineSegment(sketch, "E322", {"start": v(-46.34, -78.08) * mm, "end": v(-45.9, -77.15) * mm});
            skLineSegment(sketch, "E323", {"start": v(-45.9, -77.15) * mm, "end": v(-46.17, -76.16) * mm});
            skLineSegment(sketch, "E324", {"start": v(74.66, -52.99) * mm, "end": v(74.92, -52) * mm});
            skLineSegment(sketch, "E325", {"start": v(74.92, -52) * mm, "end": v(74.5, -51.07) * mm});
            skLineSegment(sketch, "E326", {"start": v(74.5, -51.07) * mm, "end": v(57.52, -34.1) * mm});
            skLineSegment(sketch, "E327", {"start": v(57.52, -34.1) * mm, "end": v(56.2, -32.77) * mm});
            skLineSegment(sketch, "E328", {"start": v(56.2, -32.77) * mm, "end": v(55, -31.58) * mm});
            skLineSegment(sketch, "E329", {"start": v(55, -31.58) * mm, "end": v(54.7, -31.28) * mm});
            skLineSegment(sketch, "E330", {"start": v(54.7, -31.28) * mm, "end": v(53.78, -30.85) * mm});
            skLineSegment(sketch, "E331", {"start": v(53.78, -30.85) * mm, "end": v(52.79, -31.11) * mm});
            skLineSegment(sketch, "E332", {"start": v(52.79, -31.11) * mm, "end": v(52.2, -31.96) * mm});
            skLineSegment(sketch, "E333", {"start": v(52.2, -31.96) * mm, "end": v(51.98, -32.77) * mm});
            skLineSegment(sketch, "E334", {"start": v(51.98, -32.77) * mm, "end": v(47.97, -47.74) * mm});
            skLineSegment(sketch, "E335", {"start": v(47.97, -47.74) * mm, "end": v(44.95, -58.98) * mm});
            skLineSegment(sketch, "E336", {"start": v(44.95, -58.98) * mm, "end": v(45.05, -60) * mm});
            skLineSegment(sketch, "E337", {"start": v(45.05, -60) * mm, "end": v(45.77, -60.73) * mm});
            skLineSegment(sketch, "E338", {"start": v(45.77, -60.73) * mm, "end": v(46.8, -60.82) * mm});
            skLineSegment(sketch, "E339", {"start": v(46.8, -60.82) * mm, "end": v(65.54, -55.8) * mm});
            skLineSegment(sketch, "E340", {"start": v(65.54, -55.8) * mm, "end": v(68.08, -55.12) * mm});
            skLineSegment(sketch, "E341", {"start": v(68.08, -55.12) * mm, "end": v(73.82, -53.58) * mm});
            skLineSegment(sketch, "E342", {"start": v(73.82, -53.58) * mm, "end": v(74.66, -52.99) * mm});
            skLineSegment(sketch, "E343", {"start": v(-29.5, 23.18) * mm, "end": v(-30.8, 22.04) * mm});
            skLineSegment(sketch, "E344", {"start": v(-30.8, 22.04) * mm, "end": v(-31.07, 20.34) * mm});
            skLineSegment(sketch, "E345", {"start": v(-31.07, 20.34) * mm, "end": v(-30.2, 18.86) * mm});
            skLineSegment(sketch, "E346", {"start": v(-30.2, 18.86) * mm, "end": v(-28.58, 18.27) * mm});
            skLineSegment(sketch, "E347", {"start": v(-28.58, 18.27) * mm, "end": v(27.98, 18.27) * mm});
            skLineSegment(sketch, "E348", {"start": v(27.98, 18.27) * mm, "end": v(29.6, 18.86) * mm});
            skLineSegment(sketch, "E349", {"start": v(29.6, 18.86) * mm, "end": v(30.47, 20.34) * mm});
            skLineSegment(sketch, "E350", {"start": v(30.47, 20.34) * mm, "end": v(30.2, 22.04) * mm});
            skLineSegment(sketch, "E351", {"start": v(30.2, 22.04) * mm, "end": v(28.9, 23.18) * mm});
            skLineSegment(sketch, "E352", {"start": v(28.9, 23.18) * mm, "end": v(4.5, 32.77) * mm});
            skLineSegment(sketch, "E353", {"start": v(4.5, 32.77) * mm, "end": v(0.63, 34.3) * mm});
            skLineSegment(sketch, "E354", {"start": v(0.63, 34.3) * mm, "end": v(-1.23, 34.3) * mm});
            skLineSegment(sketch, "E355", {"start": v(-1.23, 34.3) * mm, "end": v(-5.1, 32.77) * mm});
            skLineSegment(sketch, "E356", {"start": v(-5.1, 32.77) * mm, "end": v(-29.5, 23.18) * mm});
            skLineSegment(sketch, "E357", {"start": v(52, -5) * mm, "end": v(52, 5) * mm});
            skLineSegment(sketch, "E358", {"start": v(52, 5) * mm, "end": v(47, 5) * mm});
            skLineSegment(sketch, "E359", {"start": v(47, 5) * mm, "end": v(47, -5) * mm});
            skLineSegment(sketch, "E360", {"start": v(47, -5) * mm, "end": v(52, -5) * mm});
            skLineSegment(sketch, "E361", {"start": v(14.55, 39.56) * mm, "end": v(32.77, 34.67) * mm});
            skLineSegment(sketch, "E362", {"start": v(32.77, 34.67) * mm, "end": v(39.87, 32.77) * mm});
            skLineSegment(sketch, "E363", {"start": v(39.87, 32.77) * mm, "end": v(42.99, 31.93) * mm});
            skLineSegment(sketch, "E364", {"start": v(42.99, 31.93) * mm, "end": v(44, 32.02) * mm});
            skLineSegment(sketch, "E365", {"start": v(44, 32.02) * mm, "end": v(44.73, 32.75) * mm});
            skLineSegment(sketch, "E366", {"start": v(44.73, 32.75) * mm, "end": v(44.74, 32.77) * mm});
            skLineSegment(sketch, "E367", {"start": v(44.74, 32.77) * mm, "end": v(44.82, 33.77) * mm});
            skLineSegment(sketch, "E368", {"start": v(44.82, 33.77) * mm, "end": v(40.7, 49.15) * mm});
            skLineSegment(sketch, "E369", {"start": v(40.7, 49.15) * mm, "end": v(37.2, 62.21) * mm});
            skLineSegment(sketch, "E370", {"start": v(37.2, 62.21) * mm, "end": v(36.62, 63.05) * mm});
            skLineSegment(sketch, "E371", {"start": v(36.62, 63.05) * mm, "end": v(35.62, 63.32) * mm});
            skLineSegment(sketch, "E372", {"start": v(35.62, 63.32) * mm, "end": v(34.7, 62.89) * mm});
            skLineSegment(sketch, "E373", {"start": v(34.7, 62.89) * mm, "end": v(13.87, 42.06) * mm});
            skLineSegment(sketch, "E374", {"start": v(13.87, 42.06) * mm, "end": v(13.44, 41.13) * mm});
            skLineSegment(sketch, "E375", {"start": v(13.44, 41.13) * mm, "end": v(13.7, 40.15) * mm});
            skLineSegment(sketch, "E376", {"start": v(13.7, 40.15) * mm, "end": v(14.55, 39.56) * mm});
            skLineSegment(sketch, "E377", {"start": v(13.19, -42.4) * mm, "end": v(13.62, -43.33) * mm});
            skLineSegment(sketch, "E378", {"start": v(13.62, -43.33) * mm, "end": v(34.44, -64.15) * mm});
            skLineSegment(sketch, "E379", {"start": v(34.44, -64.15) * mm, "end": v(35.37, -64.58) * mm});
            skLineSegment(sketch, "E380", {"start": v(35.37, -64.58) * mm, "end": v(36.36, -64.32) * mm});
            skLineSegment(sketch, "E381", {"start": v(36.36, -64.32) * mm, "end": v(36.95, -63.48) * mm});
            skLineSegment(sketch, "E382", {"start": v(36.95, -63.48) * mm, "end": v(44.57, -35.04) * mm});
            skLineSegment(sketch, "E383", {"start": v(44.57, -35.04) * mm, "end": v(44.48, -34.01) * mm});
            skLineSegment(sketch, "E384", {"start": v(44.48, -34.01) * mm, "end": v(43.76, -33.29) * mm});
            skLineSegment(sketch, "E385", {"start": v(43.76, -33.29) * mm, "end": v(42.74, -33.2) * mm});
            skLineSegment(sketch, "E386", {"start": v(42.74, -33.2) * mm, "end": v(32.77, -35.87) * mm});
            skLineSegment(sketch, "E387", {"start": v(32.77, -35.87) * mm, "end": v(14.3, -40.82) * mm});
            skLineSegment(sketch, "E388", {"start": v(14.3, -40.82) * mm, "end": v(13.45, -41.4) * mm});
            skLineSegment(sketch, "E389", {"start": v(13.45, -41.4) * mm, "end": v(13.19, -42.4) * mm});
            skSolve(sketch);
        }
        {
            var Q0;
            Q0 = qSketchRegion(id + "F0", true);
            extrude(context, id + "F1", {"entities" : qUnion([Q0]), "depth" : 4.75 * mm, "offsetDistance" : 25 * mm});
        }
        {
            var Q0;
            Q0=makeQuery(id+"F1.opExtrude","CAP_FACE",FACE,{"disambiguationData":[OSD([sQuery(id+"F0.wireOp",EDGE,"E0"),sQuery(id+"F0.wireOp",EDGE,"E1"),sQuery(id+"F0.wireOp",EDGE,"E2"),sQuery(id+"F0.wireOp",EDGE,"E3"),sQuery(id+"F0.wireOp",EDGE,"E4"),sQuery(id+"F0.wireOp",EDGE,"E5"),sQuery(id+"F0.wireOp",EDGE,"E6"),sQuery(id+"F0.wireOp",EDGE,"E7"),sQuery(id+"F0.wireOp",EDGE,"E8"),sQuery(id+"F0.wireOp",EDGE,"E9"),sQuery(id+"F0.wireOp",EDGE,"E10"),sQuery(id+"F0.wireOp",EDGE,"E11"),sQuery(id+"F0.wireOp",EDGE,"E12"),sQuery(id+"F0.wireOp",EDGE,"E13"),sQuery(id+"F0.wireOp",EDGE,"E14"),sQuery(id+"F0.wireOp",EDGE,"E15"),sQuery(id+"F0.wireOp",EDGE,"E16"),sQuery(id+"F0.wireOp",EDGE,"E17"),sQuery(id+"F0.wireOp",EDGE,"E18"),sQuery(id+"F0.wireOp",EDGE,"E19"),sQuery(id+"F0.wireOp",EDGE,"E20"),sQuery(id+"F0.wireOp",EDGE,"E21"),sQuery(id+"F0.wireOp",EDGE,"E22"),sQuery(id+"F0.wireOp",EDGE,"E23"),sQuery(id+"F0.wireOp",EDGE,"E24"),sQuery(id+"F0.wireOp",EDGE,"E25"),sQuery(id+"F0.wireOp",EDGE,"E26"),sQuery(id+"F0.wireOp",EDGE,"E27"),sQuery(id+"F0.wireOp",EDGE,"E28"),sQuery(id+"F0.wireOp",EDGE,"E29"),sQuery(id+"F0.wireOp",EDGE,"E30"),sQuery(id+"F0.wireOp",EDGE,"E31"),sQuery(id+"F0.wireOp",EDGE,"E32"),sQuery(id+"F0.wireOp",EDGE,"E33"),sQuery(id+"F0.wireOp",EDGE,"E34"),sQuery(id+"F0.wireOp",EDGE,"E35"),sQuery(id+"F0.wireOp",EDGE,"E36"),sQuery(id+"F0.wireOp",EDGE,"E37"),sQuery(id+"F0.wireOp",EDGE,"E38"),sQuery(id+"F0.wireOp",EDGE,"E39"),sQuery(id+"F0.wireOp",EDGE,"E40"),sQuery(id+"F0.wireOp",EDGE,"E41"),sQuery(id+"F0.wireOp",EDGE,"E42"),sQuery(id+"F0.wireOp",EDGE,"E43"),sQuery(id+"F0.wireOp",EDGE,"E44"),sQuery(id+"F0.wireOp",EDGE,"E45"),sQuery(id+"F0.wireOp",EDGE,"E46"),sQuery(id+"F0.wireOp",EDGE,"E47"),sQuery(id+"F0.wireOp",EDGE,"E48"),sQuery(id+"F0.wireOp",EDGE,"E49"),sQuery(id+"F0.wireOp",EDGE,"E50"),sQuery(id+"F0.wireOp",EDGE,"E51"),sQuery(id+"F0.wireOp",EDGE,"E52"),sQuery(id+"F0.wireOp",EDGE,"E53"),sQuery(id+"F0.wireOp",EDGE,"E54"),sQuery(id+"F0.wireOp",EDGE,"E55"),sQuery(id+"F0.wireOp",EDGE,"E56"),sQuery(id+"F0.wireOp",EDGE,"E57"),sQuery(id+"F0.wireOp",EDGE,"E58"),sQuery(id+"F0.wireOp",EDGE,"E59"),sQuery(id+"F0.wireOp",EDGE,"E60"),sQuery(id+"F0.wireOp",EDGE,"E61"),sQuery(id+"F0.wireOp",EDGE,"E62"),sQuery(id+"F0.wireOp",EDGE,"E63"),sQuery(id+"F0.wireOp",EDGE,"E64"),sQuery(id+"F0.wireOp",EDGE,"E65"),sQuery(id+"F0.wireOp",EDGE,"E66"),sQuery(id+"F0.wireOp",EDGE,"E67"),sQuery(id+"F0.wireOp",EDGE,"E68"),sQuery(id+"F0.wireOp",EDGE,"E69"),sQuery(id+"F0.wireOp",EDGE,"E70"),sQuery(id+"F0.wireOp",EDGE,"E71"),sQuery(id+"F0.wireOp",EDGE,"E72"),sQuery(id+"F0.wireOp",EDGE,"E73"),sQuery(id+"F0.wireOp",EDGE,"E74"),sQuery(id+"F0.wireOp",EDGE,"E75"),sQuery(id+"F0.wireOp",EDGE,"E76"),sQuery(id+"F0.wireOp",EDGE,"E77"),sQuery(id+"F0.wireOp",EDGE,"E78"),sQuery(id+"F0.wireOp",EDGE,"E79"),sQuery(id+"F0.wireOp",EDGE,"E80"),sQuery(id+"F0.wireOp",EDGE,"E81"),sQuery(id+"F0.wireOp",EDGE,"E82"),sQuery(id+"F0.wireOp",EDGE,"E83"),sQuery(id+"F0.wireOp",EDGE,"E84"),sQuery(id+"F0.wireOp",EDGE,"E85"),sQuery(id+"F0.wireOp",EDGE,"E86"),sQuery(id+"F0.wireOp",EDGE,"E87"),sQuery(id+"F0.wireOp",EDGE,"E88"),sQuery(id+"F0.wireOp",EDGE,"E89"),sQuery(id+"F0.wireOp",EDGE,"E90"),sQuery(id+"F0.wireOp",EDGE,"E91"),sQuery(id+"F0.wireOp",EDGE,"E92"),sQuery(id+"F0.wireOp",EDGE,"E93"),sQuery(id+"F0.wireOp",EDGE,"E94"),sQuery(id+"F0.wireOp",EDGE,"E95"),sQuery(id+"F0.wireOp",EDGE,"E96"),sQuery(id+"F0.wireOp",EDGE,"E97"),sQuery(id+"F0.wireOp",EDGE,"E98"),sQuery(id+"F0.wireOp",EDGE,"E99"),sQuery(id+"F0.wireOp",EDGE,"E100"),sQuery(id+"F0.wireOp",EDGE,"E101"),sQuery(id+"F0.wireOp",EDGE,"E102"),sQuery(id+"F0.wireOp",EDGE,"E103"),sQuery(id+"F0.wireOp",EDGE,"E104"),sQuery(id+"F0.wireOp",EDGE,"E105"),sQuery(id+"F0.wireOp",EDGE,"E106"),sQuery(id+"F0.wireOp",EDGE,"E107"),sQuery(id+"F0.wireOp",EDGE,"E108"),sQuery(id+"F0.wireOp",EDGE,"E109"),sQuery(id+"F0.wireOp",EDGE,"E110"),sQuery(id+"F0.wireOp",EDGE,"E111"),sQuery(id+"F0.wireOp",EDGE,"E112"),sQuery(id+"F0.wireOp",EDGE,"E113"),sQuery(id+"F0.wireOp",EDGE,"E114"),sQuery(id+"F0.wireOp",EDGE,"E115"),sQuery(id+"F0.wireOp",EDGE,"E116"),sQuery(id+"F0.wireOp",EDGE,"E117"),sQuery(id+"F0.wireOp",EDGE,"E118"),sQuery(id+"F0.wireOp",EDGE,"E119"),sQuery(id+"F0.wireOp",EDGE,"E120"),sQuery(id+"F0.wireOp",EDGE,"E121"),sQuery(id+"F0.wireOp",EDGE,"E122"),sQuery(id+"F0.wireOp",EDGE,"E123"),sQuery(id+"F0.wireOp",EDGE,"E124"),sQuery(id+"F0.wireOp",EDGE,"E125"),sQuery(id+"F0.wireOp",EDGE,"E126"),sQuery(id+"F0.wireOp",EDGE,"E127"),sQuery(id+"F0.wireOp",EDGE,"E128"),sQuery(id+"F0.wireOp",EDGE,"E129"),sQuery(id+"F0.wireOp",EDGE,"E130"),sQuery(id+"F0.wireOp",EDGE,"E131"),sQuery(id+"F0.wireOp",EDGE,"E132"),sQuery(id+"F0.wireOp",EDGE,"E133"),sQuery(id+"F0.wireOp",EDGE,"E134"),sQuery(id+"F0.wireOp",EDGE,"E135"),sQuery(id+"F0.wireOp",EDGE,"E136"),sQuery(id+"F0.wireOp",EDGE,"E137"),sQuery(id+"F0.wireOp",EDGE,"E138"),sQuery(id+"F0.wireOp",EDGE,"E139"),sQuery(id+"F0.wireOp",EDGE,"E140"),sQuery(id+"F0.wireOp",EDGE,"E141"),sQuery(id+"F0.wireOp",EDGE,"E142"),sQuery(id+"F0.wireOp",EDGE,"E143"),sQuery(id+"F0.wireOp",EDGE,"E144"),sQuery(id+"F0.wireOp",EDGE,"E145"),sQuery(id+"F0.wireOp",EDGE,"E146"),sQuery(id+"F0.wireOp",EDGE,"E147"),sQuery(id+"F0.wireOp",EDGE,"E148"),sQuery(id+"F0.wireOp",EDGE,"E149"),sQuery(id+"F0.wireOp",EDGE,"E150"),sQuery(id+"F0.wireOp",EDGE,"E151"),sQuery(id+"F0.wireOp",EDGE,"E152"),sQuery(id+"F0.wireOp",EDGE,"E153"),sQuery(id+"F0.wireOp",EDGE,"E154"),sQuery(id+"F0.wireOp",EDGE,"E155"),sQuery(id+"F0.wireOp",EDGE,"E156"),sQuery(id+"F0.wireOp",EDGE,"E157"),sQuery(id+"F0.wireOp",EDGE,"E158"),sQuery(id+"F0.wireOp",EDGE,"E159"),sQuery(id+"F0.wireOp",EDGE,"E160"),sQuery(id+"F0.wireOp",EDGE,"E161"),sQuery(id+"F0.wireOp",EDGE,"E162"),sQuery(id+"F0.wireOp",EDGE,"E163"),sQuery(id+"F0.wireOp",EDGE,"E164"),sQuery(id+"F0.wireOp",EDGE,"E165"),sQuery(id+"F0.wireOp",EDGE,"E166"),sQuery(id+"F0.wireOp",EDGE,"E167"),sQuery(id+"F0.wireOp",EDGE,"E168"),sQuery(id+"F0.wireOp",EDGE,"E169"),sQuery(id+"F0.wireOp",EDGE,"E170"),sQuery(id+"F0.wireOp",EDGE,"E171"),sQuery(id+"F0.wireOp",EDGE,"E172"),sQuery(id+"F0.wireOp",EDGE,"E173"),sQuery(id+"F0.wireOp",EDGE,"E174"),sQuery(id+"F0.wireOp",EDGE,"E175"),sQuery(id+"F0.wireOp",EDGE,"E176"),sQuery(id+"F0.wireOp",EDGE,"E177"),sQuery(id+"F0.wireOp",EDGE,"E178"),sQuery(id+"F0.wireOp",EDGE,"E179"),sQuery(id+"F0.wireOp",EDGE,"E180"),sQuery(id+"F0.wireOp",EDGE,"E181"),sQuery(id+"F0.wireOp",EDGE,"E182"),sQuery(id+"F0.wireOp",EDGE,"E183"),sQuery(id+"F0.wireOp",EDGE,"E184"),sQuery(id+"F0.wireOp",EDGE,"E185"),sQuery(id+"F0.wireOp",EDGE,"E186"),sQuery(id+"F0.wireOp",EDGE,"E187"),sQuery(id+"F0.wireOp",EDGE,"E188"),sQuery(id+"F0.wireOp",EDGE,"E189"),sQuery(id+"F0.wireOp",EDGE,"E190"),sQuery(id+"F0.wireOp",EDGE,"E191"),sQuery(id+"F0.wireOp",EDGE,"E192"),sQuery(id+"F0.wireOp",EDGE,"E193"),sQuery(id+"F0.wireOp",EDGE,"E194"),sQuery(id+"F0.wireOp",EDGE,"E195"),sQuery(id+"F0.wireOp",EDGE,"E196"),sQuery(id+"F0.wireOp",EDGE,"E197"),sQuery(id+"F0.wireOp",EDGE,"E198"),sQuery(id+"F0.wireOp",EDGE,"E199"),sQuery(id+"F0.wireOp",EDGE,"E200"),sQuery(id+"F0.wireOp",EDGE,"E201"),sQuery(id+"F0.wireOp",EDGE,"E202"),sQuery(id+"F0.wireOp",EDGE,"E203"),sQuery(id+"F0.wireOp",EDGE,"E204"),sQuery(id+"F0.wireOp",EDGE,"E205"),sQuery(id+"F0.wireOp",EDGE,"E206"),sQuery(id+"F0.wireOp",EDGE,"E207"),sQuery(id+"F0.wireOp",EDGE,"E208"),sQuery(id+"F0.wireOp",EDGE,"E209"),sQuery(id+"F0.wireOp",EDGE,"E210"),sQuery(id+"F0.wireOp",EDGE,"E211"),sQuery(id+"F0.wireOp",EDGE,"E212"),sQuery(id+"F0.wireOp",EDGE,"E213"),sQuery(id+"F0.wireOp",EDGE,"E214"),sQuery(id+"F0.wireOp",EDGE,"E215"),sQuery(id+"F0.wireOp",EDGE,"E216"),sQuery(id+"F0.wireOp",EDGE,"E217"),sQuery(id+"F0.wireOp",EDGE,"E218"),sQuery(id+"F0.wireOp",EDGE,"E219"),sQuery(id+"F0.wireOp",EDGE,"E220"),sQuery(id+"F0.wireOp",EDGE,"E221"),sQuery(id+"F0.wireOp",EDGE,"E222"),sQuery(id+"F0.wireOp",EDGE,"E223"),sQuery(id+"F0.wireOp",EDGE,"E224"),sQuery(id+"F0.wireOp",EDGE,"E225"),sQuery(id+"F0.wireOp",EDGE,"E226"),sQuery(id+"F0.wireOp",EDGE,"E227"),sQuery(id+"F0.wireOp",EDGE,"E228"),sQuery(id+"F0.wireOp",EDGE,"E229"),sQuery(id+"F0.wireOp",EDGE,"E230"),sQuery(id+"F0.wireOp",EDGE,"E231"),sQuery(id+"F0.wireOp",EDGE,"E232"),sQuery(id+"F0.wireOp",EDGE,"E233"),sQuery(id+"F0.wireOp",EDGE,"E234"),sQuery(id+"F0.wireOp",EDGE,"E235"),sQuery(id+"F0.wireOp",EDGE,"E236"),sQuery(id+"F0.wireOp",EDGE,"E237"),sQuery(id+"F0.wireOp",EDGE,"E238"),sQuery(id+"F0.wireOp",EDGE,"E239"),sQuery(id+"F0.wireOp",EDGE,"E240"),sQuery(id+"F0.wireOp",EDGE,"E241"),sQuery(id+"F0.wireOp",EDGE,"E242"),sQuery(id+"F0.wireOp",EDGE,"E243"),sQuery(id+"F0.wireOp",EDGE,"E244"),sQuery(id+"F0.wireOp",EDGE,"E245"),sQuery(id+"F0.wireOp",EDGE,"E246"),sQuery(id+"F0.wireOp",EDGE,"E247"),sQuery(id+"F0.wireOp",EDGE,"E248"),sQuery(id+"F0.wireOp",EDGE,"E249"),sQuery(id+"F0.wireOp",EDGE,"E250"),sQuery(id+"F0.wireOp",EDGE,"E251"),sQuery(id+"F0.wireOp",EDGE,"E252"),sQuery(id+"F0.wireOp",EDGE,"E253"),sQuery(id+"F0.wireOp",EDGE,"E254"),sQuery(id+"F0.wireOp",EDGE,"E255"),sQuery(id+"F0.wireOp",EDGE,"E256"),sQuery(id+"F0.wireOp",EDGE,"E257"),sQuery(id+"F0.wireOp",EDGE,"E258"),sQuery(id+"F0.wireOp",EDGE,"E259"),sQuery(id+"F0.wireOp",EDGE,"E260"),sQuery(id+"F0.wireOp",EDGE,"E261"),sQuery(id+"F0.wireOp",EDGE,"E262"),sQuery(id+"F0.wireOp",EDGE,"E263"),sQuery(id+"F0.wireOp",EDGE,"E264"),sQuery(id+"F0.wireOp",EDGE,"E265"),sQuery(id+"F0.wireOp",EDGE,"E266"),sQuery(id+"F0.wireOp",EDGE,"E267"),sQuery(id+"F0.wireOp",EDGE,"E268"),sQuery(id+"F0.wireOp",EDGE,"E269"),sQuery(id+"F0.wireOp",EDGE,"E270"),sQuery(id+"F0.wireOp",EDGE,"E271"),sQuery(id+"F0.wireOp",EDGE,"E272"),sQuery(id+"F0.wireOp",EDGE,"E273"),sQuery(id+"F0.wireOp",EDGE,"E274"),sQuery(id+"F0.wireOp",EDGE,"E275"),sQuery(id+"F0.wireOp",EDGE,"E276"),sQuery(id+"F0.wireOp",EDGE,"E277"),sQuery(id+"F0.wireOp",EDGE,"E278"),sQuery(id+"F0.wireOp",EDGE,"E279"),sQuery(id+"F0.wireOp",EDGE,"E280"),sQuery(id+"F0.wireOp",EDGE,"E281"),sQuery(id+"F0.wireOp",EDGE,"E282"),sQuery(id+"F0.wireOp",EDGE,"E283"),sQuery(id+"F0.wireOp",EDGE,"E284"),sQuery(id+"F0.wireOp",EDGE,"E285"),sQuery(id+"F0.wireOp",EDGE,"E286"),sQuery(id+"F0.wireOp",EDGE,"E287"),sQuery(id+"F0.wireOp",EDGE,"E288"),sQuery(id+"F0.wireOp",EDGE,"E289"),sQuery(id+"F0.wireOp",EDGE,"E290"),sQuery(id+"F0.wireOp",EDGE,"E291"),sQuery(id+"F0.wireOp",EDGE,"E292"),sQuery(id+"F0.wireOp",EDGE,"E293"),sQuery(id+"F0.wireOp",EDGE,"E294"),sQuery(id+"F0.wireOp",EDGE,"E295"),sQuery(id+"F0.wireOp",EDGE,"E296"),sQuery(id+"F0.wireOp",EDGE,"E297"),sQuery(id+"F0.wireOp",EDGE,"E298"),sQuery(id+"F0.wireOp",EDGE,"E299"),sQuery(id+"F0.wireOp",EDGE,"E300"),sQuery(id+"F0.wireOp",EDGE,"E301"),sQuery(id+"F0.wireOp",EDGE,"E302"),sQuery(id+"F0.wireOp",EDGE,"E303"),sQuery(id+"F0.wireOp",EDGE,"E304"),sQuery(id+"F0.wireOp",EDGE,"E305"),sQuery(id+"F0.wireOp",EDGE,"E306"),sQuery(id+"F0.wireOp",EDGE,"E307"),sQuery(id+"F0.wireOp",EDGE,"E308"),sQuery(id+"F0.wireOp",EDGE,"E309"),sQuery(id+"F0.wireOp",EDGE,"E310"),sQuery(id+"F0.wireOp",EDGE,"E311"),sQuery(id+"F0.wireOp",EDGE,"E312"),sQuery(id+"F0.wireOp",EDGE,"E313"),sQuery(id+"F0.wireOp",EDGE,"E314"),sQuery(id+"F0.wireOp",EDGE,"E315"),sQuery(id+"F0.wireOp",EDGE,"E316"),sQuery(id+"F0.wireOp",EDGE,"E317"),sQuery(id+"F0.wireOp",EDGE,"E318"),sQuery(id+"F0.wireOp",EDGE,"E319"),sQuery(id+"F0.wireOp",EDGE,"E320"),sQuery(id+"F0.wireOp",EDGE,"E321"),sQuery(id+"F0.wireOp",EDGE,"E322"),sQuery(id+"F0.wireOp",EDGE,"E323"),sQuery(id+"F0.wireOp",EDGE,"E324"),sQuery(id+"F0.wireOp",EDGE,"E325"),sQuery(id+"F0.wireOp",EDGE,"E326"),sQuery(id+"F0.wireOp",EDGE,"E327"),sQuery(id+"F0.wireOp",EDGE,"E328"),sQuery(id+"F0.wireOp",EDGE,"E329"),sQuery(id+"F0.wireOp",EDGE,"E330"),sQuery(id+"F0.wireOp",EDGE,"E331"),sQuery(id+"F0.wireOp",EDGE,"E332"),sQuery(id+"F0.wireOp",EDGE,"E333"),sQuery(id+"F0.wireOp",EDGE,"E334"),sQuery(id+"F0.wireOp",EDGE,"E335"),sQuery(id+"F0.wireOp",EDGE,"E336"),sQuery(id+"F0.wireOp",EDGE,"E337"),sQuery(id+"F0.wireOp",EDGE,"E338"),sQuery(id+"F0.wireOp",EDGE,"E339"),sQuery(id+"F0.wireOp",EDGE,"E340"),sQuery(id+"F0.wireOp",EDGE,"E341"),sQuery(id+"F0.wireOp",EDGE,"E342"),sQuery(id+"F0.wireOp",EDGE,"E343"),sQuery(id+"F0.wireOp",EDGE,"E344"),sQuery(id+"F0.wireOp",EDGE,"E345"),sQuery(id+"F0.wireOp",EDGE,"E346"),sQuery(id+"F0.wireOp",EDGE,"E347"),sQuery(id+"F0.wireOp",EDGE,"E348"),sQuery(id+"F0.wireOp",EDGE,"E349"),sQuery(id+"F0.wireOp",EDGE,"E350"),sQuery(id+"F0.wireOp",EDGE,"E351"),sQuery(id+"F0.wireOp",EDGE,"E352"),sQuery(id+"F0.wireOp",EDGE,"E353"),sQuery(id+"F0.wireOp",EDGE,"E354"),sQuery(id+"F0.wireOp",EDGE,"E355"),sQuery(id+"F0.wireOp",EDGE,"E356"),sQuery(id+"F0.wireOp",EDGE,"E357"),sQuery(id+"F0.wireOp",EDGE,"E358"),sQuery(id+"F0.wireOp",EDGE,"E359"),sQuery(id+"F0.wireOp",EDGE,"E360"),sQuery(id+"F0.wireOp",EDGE,"E361"),sQuery(id+"F0.wireOp",EDGE,"E362"),sQuery(id+"F0.wireOp",EDGE,"E363"),sQuery(id+"F0.wireOp",EDGE,"E364"),sQuery(id+"F0.wireOp",EDGE,"E365"),sQuery(id+"F0.wireOp",EDGE,"E366"),sQuery(id+"F0.wireOp",EDGE,"E367"),sQuery(id+"F0.wireOp",EDGE,"E368"),sQuery(id+"F0.wireOp",EDGE,"E369"),sQuery(id+"F0.wireOp",EDGE,"E370"),sQuery(id+"F0.wireOp",EDGE,"E371"),sQuery(id+"F0.wireOp",EDGE,"E372"),sQuery(id+"F0.wireOp",EDGE,"E373"),sQuery(id+"F0.wireOp",EDGE,"E374"),sQuery(id+"F0.wireOp",EDGE,"E375"),sQuery(id+"F0.wireOp",EDGE,"E376"),sQuery(id+"F0.wireOp",EDGE,"E377"),sQuery(id+"F0.wireOp",EDGE,"E378"),sQuery(id+"F0.wireOp",EDGE,"E379"),sQuery(id+"F0.wireOp",EDGE,"E380"),sQuery(id+"F0.wireOp",EDGE,"E381"),sQuery(id+"F0.wireOp",EDGE,"E382"),sQuery(id+"F0.wireOp",EDGE,"E383"),sQuery(id+"F0.wireOp",EDGE,"E384"),sQuery(id+"F0.wireOp",EDGE,"E385"),sQuery(id+"F0.wireOp",EDGE,"E386"),sQuery(id+"F0.wireOp",EDGE,"E387"),sQuery(id+"F0.wireOp",EDGE,"E388"),sQuery(id+"F0.wireOp",EDGE,"E389")])],"isStart":false});
            var sketch = newSketch(context, id + "F2", { "sketchPlane" : qUnion([Q0])});
            skCircle(sketch, "E390", {"center": v(-10, 10) * mm, "radius": 1.52 * mm});
            skCircle(sketch, "E391", {"center": v(-10, -10) * mm, "radius": 1.52 * mm});
            skCircle(sketch, "E392", {"center": v(-104.5, 104.5) * mm, "radius": 1.65 * mm});
            skCircle(sketch, "E393", {"center": v(-104.5, -104.5) * mm, "radius": 1.65 * mm});
            skCircle(sketch, "E394", {"center": v(-44.45, 20.8) * mm, "radius": 3.56 * mm});
            skCircle(sketch, "E395", {"center": v(-44.45, -20.8) * mm, "radius": 2.55 * mm});
            skSolve(sketch);
        }
        {
            var Q0;
            Q0 = qSketchRegion(id + "F2", true);
            extrude(context, id + "F3", {"entities" : qUnion([Q0]), "operationType" : NewBodyOperationType.REMOVE, "endBound" : BoundingType.THROUGH_ALL, "oppositeDirection" : true, "depth" : 25 * mm, "offsetDistance" : 25 * mm});
        }
    });
